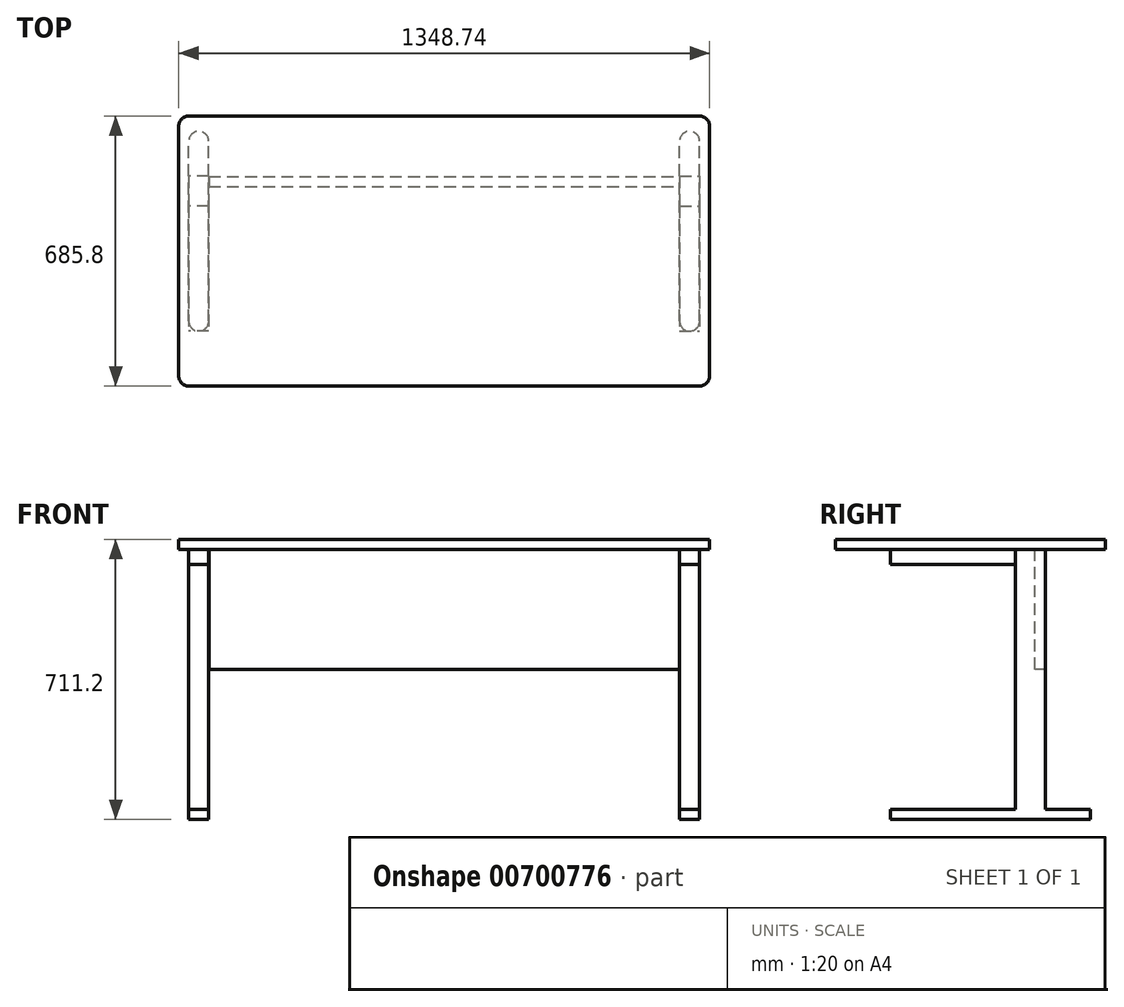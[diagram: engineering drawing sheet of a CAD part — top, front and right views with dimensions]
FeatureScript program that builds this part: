
annotation { "Feature Type Name" : "Feature", "Feature Type Description" : "" }
export const myFeature = defineFeature(function(context is Context, id is Id, definition is map)
    precondition{}
    {
        {
            var Q0;
            Q0=qCreatedBy(makeId("Top.planeOp"),FACE);
            var sketch = newSketch(context, id + "F0", { "sketchPlane" : qUnion([Q0])});
            skLineSegment(sketch, "E0.bottom", {"start": v(648.97, -342.9) * mm, "end": v(-648.97, -342.9) * mm});
            skLineSegment(sketch, "E0.top", {"start": v(648.97, 342.9) * mm, "end": v(-648.97, 342.9) * mm});
            skLineSegment(sketch, "E0.left", {"start": v(674.37, -317.5) * mm, "end": v(674.37, 317.5) * mm});
            skLineSegment(sketch, "E0.right", {"start": v(-674.37, -317.5) * mm, "end": v(-674.37, 317.5) * mm});
            skPoint(sketch, "E0.middle", {"position": v(0, 0) * mm});
            skLineSegment(sketch, "E1", {"start": v(0, -342.9) * mm, "end": v(0, 342.9) * mm});
            skPoint(sketch, "E2.visualSharp", {"position": v(-674.37, -342.9) * mm});
            skArc(sketch, "E2.filletArc", {"start": v(-674.37, -317.5) * mm, "mid": v(-666.93, -335.46) * mm, "end": v(-648.97, -342.9) * mm});
            skPoint(sketch, "E3.visualSharp", {"position": v(-674.37, 342.9) * mm});
            skArc(sketch, "E3.filletArc", {"start": v(-648.97, 342.9) * mm, "mid": v(-666.93, 335.46) * mm, "end": v(-674.37, 317.5) * mm});
            skPoint(sketch, "E4.visualSharp", {"position": v(674.37, 342.9) * mm});
            skArc(sketch, "E4.filletArc", {"start": v(674.37, 317.5) * mm, "mid": v(666.93, 335.46) * mm, "end": v(648.97, 342.9) * mm});
            skPoint(sketch, "E5.visualSharp", {"position": v(674.37, -342.9) * mm});
            skArc(sketch, "E5.filletArc", {"start": v(648.97, -342.9) * mm, "mid": v(666.93, -335.46) * mm, "end": v(674.37, -317.5) * mm});
            skSolve(sketch);
        }
        {
            var Q0;
            Q0 = qSketchRegion(id + "F0", true);
            extrude(context, id + "F1", {"entities" : qUnion([Q0]), "depth" : 25.4 * mm, "offsetDistance" : 25.4 * mm});
        }
        {
            var Q0;
            Q0=qCreatedBy(makeId("Top.planeOp"),FACE);
            var sketch = newSketch(context, id + "F2", { "sketchPlane" : qUnion([Q0])});
            skLineSegment(sketch, "E6.bottom", {"start": v(-598.17, 114.3) * mm, "end": v(-648.97, 114.3) * mm});
            skLineSegment(sketch, "E6.top", {"start": v(-598.17, -203.2) * mm, "end": v(-648.97, -203.2) * mm});
            skLineSegment(sketch, "E6.left", {"start": v(-598.17, 114.3) * mm, "end": v(-598.17, -203.2) * mm});
            skLineSegment(sketch, "E6.right", {"start": v(-648.97, 114.3) * mm, "end": v(-648.97, -203.2) * mm});
            skPoint(sketch, "E6.middle", {"position": v(-623.57, -44.45) * mm});
            skPoint(sketch, "E7.middle", {"position": v(623.57, -44.45) * mm});
            skLineSegment(sketch, "E8.MirrorCS", {"start": v(598.17, 114.3) * mm, "end": v(598.17, -203.2) * mm});
            skLineSegment(sketch, "E9.MirrorCS", {"start": v(598.17, -203.2) * mm, "end": v(648.97, -203.2) * mm});
            skLineSegment(sketch, "E10.MirrorCS", {"start": v(648.97, 114.3) * mm, "end": v(648.97, -203.2) * mm});
            skLineSegment(sketch, "E11.MirrorCS", {"start": v(598.17, 114.3) * mm, "end": v(648.97, 114.3) * mm});
            skSolve(sketch);
        }
        {
            var Q0;
            Q0 = qSketchRegion(id + "F2", true);
            extrude(context, id + "F3", {"entities" : qUnion([Q0]), "operationType" : NewBodyOperationType.ADD, "oppositeDirection" : true, "depth" : 38.1 * mm, "offsetDistance" : 25.4 * mm});
        }
        {
            var Q0;
            {var subQ0=sQuery(id+"F0.wireOp",EDGE,"E0.right");Q0=makeQuery(id+"F0.imprint","IMPRINT",FACE,{"disambiguationData":[TD([[makeQuery(id+"F0.imprint","IMPRINT",EDGE,{"derivedFrom":subQ0}),-1.0]])]});}
            var sketch = newSketch(context, id + "F4", { "sketchPlane" : qUnion([Q0])});
            skLineSegment(sketch, "E12.bottom", {"start": v(-598.13, 190.32) * mm, "end": v(-648.93, 190.32) * mm});
            skLineSegment(sketch, "E12.top", {"start": v(-598.13, 114.12) * mm, "end": v(-648.93, 114.12) * mm});
            skLineSegment(sketch, "E12.left", {"start": v(-598.13, 190.32) * mm, "end": v(-598.13, 114.12) * mm});
            skLineSegment(sketch, "E12.right", {"start": v(-648.93, 190.32) * mm, "end": v(-648.93, 114.12) * mm});
            skPoint(sketch, "E12.middle", {"position": v(-623.53, 152.22) * mm});
            skLineSegment(sketch, "E13.MirrorCS", {"start": v(598.13, 190.32) * mm, "end": v(598.13, 114.12) * mm});
            skLineSegment(sketch, "E14.MirrorCS", {"start": v(598.13, 114.12) * mm, "end": v(648.93, 114.12) * mm});
            skLineSegment(sketch, "E15.MirrorCS", {"start": v(648.93, 190.32) * mm, "end": v(648.93, 114.12) * mm});
            skLineSegment(sketch, "E16.MirrorCS", {"start": v(598.13, 190.32) * mm, "end": v(648.93, 190.32) * mm});
            skSolve(sketch);
        }
        {
            var Q0;
            Q0 = qSketchRegion(id + "F4", true);
            extrude(context, id + "F5", {"entities" : qUnion([Q0]), "operationType" : NewBodyOperationType.ADD, "oppositeDirection" : true, "depth" : 660.4 * mm, "offsetDistance" : 25.4 * mm});
        }
        {
            var Q0;
            Q0=qCreatedBy(makeId("Top.planeOp"),FACE);
            var sketch = newSketch(context, id + "F6", { "sketchPlane" : qUnion([Q0])});
            skLineSegment(sketch, "E17.bottom", {"start": v(-597.7, 188.93) * mm, "end": v(597.7, 188.93) * mm});
            skLineSegment(sketch, "E17.top", {"start": v(-597.7, 163.53) * mm, "end": v(597.7, 163.53) * mm});
            skLineSegment(sketch, "E17.left", {"start": v(-597.7, 188.93) * mm, "end": v(-597.7, 163.53) * mm});
            skLineSegment(sketch, "E17.right", {"start": v(597.7, 188.93) * mm, "end": v(597.7, 163.53) * mm});
            skSolve(sketch);
        }
        {
            var Q0;
            Q0 = qSketchRegion(id + "F6", true);
            extrude(context, id + "F7", {"entities" : qUnion([Q0]), "operationType" : NewBodyOperationType.ADD, "oppositeDirection" : true, "depth" : 304.8 * mm, "offsetDistance" : 25.4 * mm});
        }
        {
            var Q0;
            Q0=makeQuery(id+"F5.opExtrude","CAP_FACE",FACE,{"disambiguationData":[OSD([sQuery(id+"F4.wireOp",EDGE,"E12.bottom"),sQuery(id+"F4.wireOp",EDGE,"E12.top"),sQuery(id+"F4.wireOp",EDGE,"E12.left"),sQuery(id+"F4.wireOp",EDGE,"E12.right")])],"isStart":false});
            var sketch = newSketch(context, id + "F8", { "sketchPlane" : qUnion([Q0])});
            skLineSegment(sketch, "E18.bottom", {"start": v(-623.53, 203.56) * mm, "end": v(-623.53, 203.56) * mm});
            skLineSegment(sketch, "E18.top", {"start": v(-623.53, -304.44) * mm, "end": v(-623.53, -304.44) * mm});
            skLineSegment(sketch, "E18.left", {"start": v(-648.93, 178.16) * mm, "end": v(-648.93, -279.04) * mm});
            skLineSegment(sketch, "E18.right", {"start": v(-598.13, 178.16) * mm, "end": v(-598.13, -279.04) * mm});
            skPoint(sketch, "E18.middle", {"position": v(-623.53, -50.44) * mm});
            skPoint(sketch, "E19", {"position": v(-623.53, -114.12) * mm});
            skLineSegment(sketch, "E20.MirrorCS", {"start": v(598.13, 178.16) * mm, "end": v(598.13, -279.04) * mm});
            skLineSegment(sketch, "E21.MirrorCS", {"start": v(623.53, 203.56) * mm, "end": v(623.53, 203.56) * mm});
            skLineSegment(sketch, "E22.MirrorCS", {"start": v(648.93, 178.16) * mm, "end": v(648.93, -279.04) * mm});
            skLineSegment(sketch, "E23.MirrorCS", {"start": v(623.53, -304.44) * mm, "end": v(623.53, -304.44) * mm});
            skPoint(sketch, "E24.visualSharp", {"position": v(-648.93, 203.56) * mm});
            skArc(sketch, "E24.filletArc", {"start": v(-623.53, 203.56) * mm, "mid": v(-641.5, 196.12) * mm, "end": v(-648.93, 178.16) * mm});
            skPoint(sketch, "E25.visualSharp", {"position": v(-598.13, 203.56) * mm});
            skArc(sketch, "E25.filletArc", {"start": v(-598.13, 178.16) * mm, "mid": v(-605.57, 196.12) * mm, "end": v(-623.53, 203.56) * mm});
            skPoint(sketch, "E26.visualSharp", {"position": v(-598.13, -304.44) * mm});
            skArc(sketch, "E26.filletArc", {"start": v(-623.53, -304.44) * mm, "mid": v(-605.57, -297) * mm, "end": v(-598.13, -279.04) * mm});
            skPoint(sketch, "E27.visualSharp", {"position": v(-648.93, -304.44) * mm});
            skArc(sketch, "E27.filletArc", {"start": v(-648.93, -279.04) * mm, "mid": v(-641.5, -297) * mm, "end": v(-623.53, -304.44) * mm});
            skPoint(sketch, "E28.visualSharp", {"position": v(598.13, -304.44) * mm});
            skArc(sketch, "E28.filletArc", {"start": v(598.13, -279.04) * mm, "mid": v(605.57, -297) * mm, "end": v(623.53, -304.44) * mm});
            skPoint(sketch, "E29.visualSharp", {"position": v(648.93, -304.44) * mm});
            skArc(sketch, "E29.filletArc", {"start": v(623.53, -304.44) * mm, "mid": v(641.5, -297) * mm, "end": v(648.93, -279.04) * mm});
            skPoint(sketch, "E30.visualSharp", {"position": v(598.13, 203.56) * mm});
            skArc(sketch, "E30.filletArc", {"start": v(623.53, 203.56) * mm, "mid": v(605.57, 196.12) * mm, "end": v(598.13, 178.16) * mm});
            skPoint(sketch, "E31.visualSharp", {"position": v(648.93, 203.56) * mm});
            skArc(sketch, "E31.filletArc", {"start": v(648.93, 178.16) * mm, "mid": v(641.5, 196.12) * mm, "end": v(623.53, 203.56) * mm});
            skSolve(sketch);
        }
        {
            var Q0;
            Q0 = qSketchRegion(id + "F8", true);
            extrude(context, id + "F9", {"entities" : qUnion([Q0]), "operationType" : NewBodyOperationType.ADD, "depth" : 25.4 * mm, "offsetDistance" : 25.4 * mm});
        }
    });
